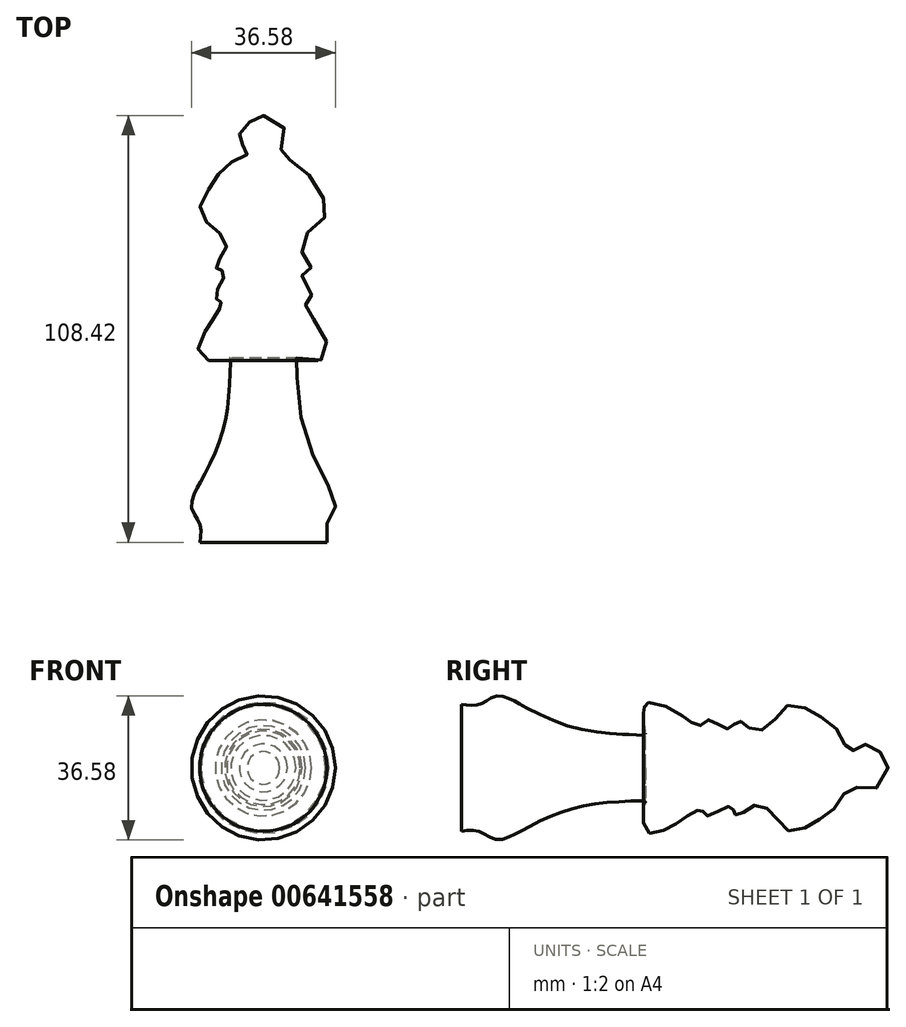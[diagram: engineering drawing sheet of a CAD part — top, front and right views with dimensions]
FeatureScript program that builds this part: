
annotation { "Feature Type Name" : "Feature", "Feature Type Description" : "" }
export const myFeature = defineFeature(function(context is Context, id is Id, definition is map)
    precondition{}
    {
        {
            var Q0;
            Q0=qCreatedBy(makeId("Top.planeOp"),FACE);
            var sketch = newSketch(context, id + "F0", { "sketchPlane" : qUnion([Q0])});
            skLineSegment(sketch, "E0", {"start": v(-40.03, 64.77) * mm, "end": v(-40.03, -59.56) * mm});
            skLineSegment(sketch, "E1", {"start": v(-40.03, -49.87) * mm, "end": v(-23.88, -49.87) * mm});
            skFitSpline(sketch, "E2", {"points": [v(-23.88, -49.87) * mm, v(-23.88, -45.26) * mm, v(-21.8, -41.1) * mm, v(-23.88, -34.88) * mm, v(-30.34, -18.96) * mm, v(-31.72, -3.74) * mm, v(-31.5, -3.05) * mm, v(-23.88, -3.05) * mm, v(-26.19, 5.26) * mm, v(-28.26, 8.26) * mm, v(-29.19, 11.26) * mm, v(-27.8, 12.4) * mm, v(-30.1, 17.71) * mm, v(-29.65, 19.1) * mm, v(-27.8, 20.25) * mm, v(-30.57, 24.63) * mm, v(-27.57, 29.94) * mm, v(-23.88, 33.86) * mm, v(-26.42, 40.32) * mm, v(-31.96, 46.78) * mm, v(-35.88, 48.85) * mm, v(-34.03, 54.16) * mm, v(-40.03, 58.54) * mm, v(-40.03, 58.31) * mm], "startDerivative": vector(-18.45, 115.41) * mm, "endDerivative": vector(14.43, -32.83) * mm});
            skSolve(sketch);
        }
        {
            var Q0;
            {var subQ4=sQuery(id+"F0.wireOp",EDGE,"E1");Q0=makeQuery(id+"F0.imprint","IMPRINT",FACE,{"disambiguationData":[TD([[makeQuery(id+"F0.imprint","IMPRINT",EDGE,{"derivedFrom":subQ4}),1.0]])]});}
            var Q1;
            Q1=sQuery(id+"F0.wireOp",EDGE,"E0");
            revolve(context, id + "F1", {"entities" : qUnion([Q0]), "axis" : qUnion([Q1]), "revolveType" : RevolveType.FULL});
        }
    });
